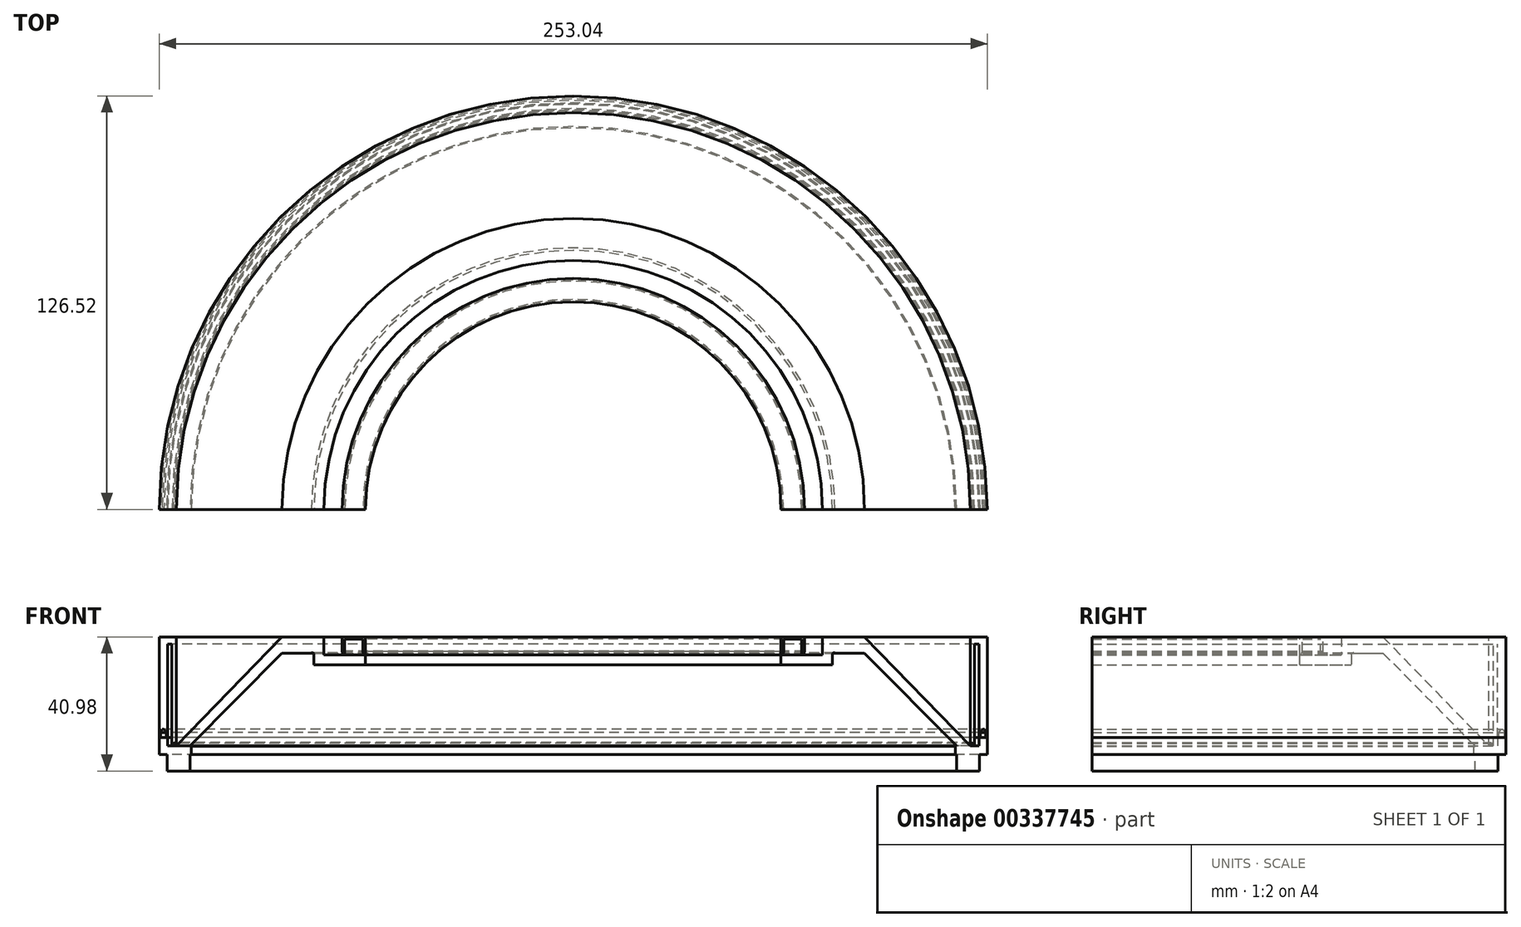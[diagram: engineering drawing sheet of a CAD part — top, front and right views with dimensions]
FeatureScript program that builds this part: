
annotation { "Feature Type Name" : "Feature", "Feature Type Description" : "" }
export const myFeature = defineFeature(function(context is Context, id is Id, definition is map)
    precondition{}
    {
        {
            var Q0;
            Q0=qCreatedBy(makeId("Top.planeOp"),FACE);
            var sketch = newSketch(context, id + "F0", { "sketchPlane" : qUnion([Q0])});
            skCircle(sketch, "E0", {"center": v(0, 0) * mm, "radius": 126.52 * mm});
            skCircle(sketch, "E1", {"center": v(0, 0) * mm, "radius": 124.16 * mm});
            skSolve(sketch);
        }
        {
            var Q0;
            Q0=makeQuery(id+"F0.imprint","IMPRINT",FACE,{"disambiguationData":[TD([[makeQuery(id+"F0.imprint","IMPRINT",EDGE,{"derivedFrom":sQuery(id+"F0.wireOp",EDGE,"E0")}),1.0]])]});
            extrude(context, id + "F1", {"entities" : qUnion([Q0]), "depth" : 2.54 * mm});
        }
        {
            var Q0;
            Q0=makeQuery(id+"F1.opExtrude","CAP_FACE",FACE,{"disambiguationData":[OSD([sQuery(id+"F0.wireOp",EDGE,"E0"),sQuery(id+"F0.wireOp",EDGE,"E1")])],"isStart":true});
            var sketch = newSketch(context, id + "F2", { "sketchPlane" : qUnion([Q0])});
            skCircle(sketch, "E2", {"center": v(0, 0) * mm, "radius": 117.14 * mm});
            skSolve(sketch);
        }
        {
            var Q0;
            Q0=makeQuery(id+"F2.imprint","IMPRINT",FACE,{"disambiguationData":[TD([[makeQuery(id+"F2.imprint","IMPRINT",EDGE,{"derivedFrom":sQuery(id+"F2.wireOp",EDGE,"E2")}),-1.0]])]});
            extrude(context, id + "F3", {"entities" : qUnion([Q0]), "depth" : 5.08 * mm});
        }
        {
            var Q0;
            Q0=makeQuery(id+"F1.opExtrude","CAP_FACE",FACE,{"disambiguationData":[OSD([sQuery(id+"F0.wireOp",EDGE,"E0"),sQuery(id+"F0.wireOp",EDGE,"E1")])],"isStart":false});
            var sketch = newSketch(context, id + "F4", { "sketchPlane" : qUnion([Q0])});
            skCircle(sketch, "E3", {"center": v(0, 0) * mm, "radius": 125.74 * mm});
            skCircle(sketch, "E4", {"center": v(0, 0) * mm, "radius": 116.73 * mm});
            skSolve(sketch);
        }
        {
            var Q0;
            Q0 = qSketchRegion(id + "F4", true);
            extrude(context, id + "F5", {"entities" : qUnion([Q0]), "oppositeDirection" : true, "depth" : 2.54 * mm});
        }
        {
            var Q0;
            Q0=qCreatedBy(makeId("Front.planeOp"),FACE);
            var sketch = newSketch(context, id + "F6", { "sketchPlane" : qUnion([Q0])});
            skLineSegment(sketch, "E5.bottom", {"start": v(-161.42, 99.97) * mm, "end": v(188.15, 99.97) * mm});
            skLineSegment(sketch, "E5.top", {"start": v(-161.42, -119.89) * mm, "end": v(188.15, -119.89) * mm});
            skLineSegment(sketch, "E5.left", {"start": v(-161.42, 99.97) * mm, "end": v(-161.42, -119.89) * mm});
            skLineSegment(sketch, "E5.right", {"start": v(188.15, 99.97) * mm, "end": v(188.15, -119.89) * mm});
            skSolve(sketch);
        }
        {
            var Q0;
            Q0 = qSketchRegion(id + "F6", true);
            extrude(context, id + "F7", {"entities" : qUnion([Q0]), "operationType" : NewBodyOperationType.REMOVE, "depth" : 152.4 * mm});
        }
        {
            var Q0;
            Q0=qCreatedBy(makeId("Front.planeOp"),FACE);
            var sketch = newSketch(context, id + "F8", { "sketchPlane" : qUnion([Q0])});
            skLineSegment(sketch, "E6", {"start": v(0, 0) * mm, "end": v(0, 30.48) * mm});
            skLineSegment(sketch, "E7", {"start": v(63.5, 30.48) * mm, "end": v(76.2, 30.44) * mm});
            skLineSegment(sketch, "E8", {"start": v(76.2, 30.44) * mm, "end": v(76.2, 35.9) * mm});
            skLineSegment(sketch, "E9.1", {"start": v(79.25, 27.38) * mm, "end": v(79.25, 30.55) * mm});
            skLineSegment(sketch, "E9.2", {"start": v(63.5, 27.43) * mm, "end": v(79.25, 27.38) * mm});
            skLineSegment(sketch, "E10", {"start": v(119.67, 0) * mm, "end": v(121.44, 2.5) * mm});
            skLineSegment(sketch, "E11", {"start": v(63.5, 27.43) * mm, "end": v(63.5, 30.48) * mm});
            skLineSegment(sketch, "E12", {"start": v(0, 0) * mm, "end": v(0, -4.78) * mm});
            skPoint(sketch, "E13.visualSharp", {"position": v(79.25, 31.44) * mm});
            skArc(sketch, "E13.filletArc", {"start": v(80.01, 30.99) * mm, "mid": v(79.5, 31) * mm, "end": v(79.25, 30.55) * mm});
            skPoint(sketch, "E14.visualSharp", {"position": v(76.2, 36.79) * mm});
            skLineSegment(sketch, "E15", {"start": v(76.2, 35.9) * mm, "end": v(89.01, 35.9) * mm});
            skLineSegment(sketch, "E16", {"start": v(89.01, 35.9) * mm, "end": v(121.44, 2.5) * mm});
            skLineSegment(sketch, "E17", {"start": v(80.01, 30.99) * mm, "end": v(89.01, 30.96) * mm});
            skLineSegment(sketch, "E18", {"start": v(89.01, 30.96) * mm, "end": v(119.67, 0) * mm});
            skSolve(sketch);
        }
        {
            var Q0;
            Q0 = qSketchRegion(id + "F8", true);
            var Q1;
            Q1=sQuery(id+"F8.wireOp",EDGE,"E6");
            revolve(context, id + "F9", {"operationType" : NewBodyOperationType.ADD, "entities" : qUnion([Q0]), "axis" : qUnion([Q1]), "revolveType" : RevolveType.ONE_DIRECTION, "angle" : 180 * degree});
        }
        {
            var Q0;
            Q0=qCreatedBy(makeId("Front.planeOp"),FACE);
            var sketch = newSketch(context, id + "F10", { "sketchPlane" : qUnion([Q0])});
            skLineSegment(sketch, "E19", {"start": v(123.98, 2.54) * mm, "end": v(126.52, 2.54) * mm});
            skLineSegment(sketch, "E20", {"start": v(126.52, 2.54) * mm, "end": v(126.52, 5.13) * mm});
            skLineSegment(sketch, "E21", {"start": v(123.98, 2.54) * mm, "end": v(123.98, 5.13) * mm});
            skLineSegment(sketch, "E22", {"start": v(126.52, 5.13) * mm, "end": v(123.98, 5.13) * mm});
            skLineSegment(sketch, "E23", {"start": v(0, -2.32) * mm, "end": v(0, -16.42) * mm});
            skSolve(sketch);
        }
        {
            var Q0;
            Q0 = qSketchRegion(id + "F10", true);
            var Q1;
            Q1=sQuery(id+"F10.wireOp",EDGE,"E23");
            revolve(context, id + "F11", {"entities" : qUnion([Q0]), "axis" : qUnion([Q1]), "revolveType" : RevolveType.ONE_DIRECTION, "oppositeDirection" : true, "angle" : 180 * degree});
        }
        {
            var Q0;
            {var subQ0=sQuery(id+"F2.wireOp",EDGE,"E2");var subQ1=sQuery(id+"F0.wireOp",EDGE,"E1");Q0=makeQuery(id+"F7.boolean.opBoolean","COPY",FACE,{"disambiguationData":[TD([makeQuery(id+"F3.opExtrude","SWEPT_FACE",FACE,{"disambiguationData":[OSD([subQ0])]}),makeQuery(id+"F3.opExtrude","CAP_FACE",FACE,{"disambiguationData":[OSD([subQ1,subQ0])],"isStart":true}),makeQuery(id+"F3.opExtrude","CAP_FACE",FACE,{"disambiguationData":[OSD([subQ1,subQ0])],"isStart":false}),makeQuery(id+"F3.opExtrude","SWEPT_FACE",FACE,{"disambiguationData":[OSD([subQ1])]})]),OD(1.0)],"derivedFrom":makeQuery(id+"F7.opExtrude","CAP_FACE",FACE,{"disambiguationData":[OSD([sQuery(id+"F6.wireOp",EDGE,"E5.bottom"),sQuery(id+"F6.wireOp",EDGE,"E5.top"),sQuery(id+"F6.wireOp",EDGE,"E5.left"),sQuery(id+"F6.wireOp",EDGE,"E5.right")])],"isStart":true})});}
            var sketch = newSketch(context, id + "F12", { "sketchPlane" : qUnion([Q0])});
            skLineSegment(sketch, "E24", {"start": v(117.14, 0) * mm, "end": v(117.14, -5.08) * mm});
            skLineSegment(sketch, "E25", {"start": v(117.14, -5.08) * mm, "end": v(124.16, -5.08) * mm});
            skLineSegment(sketch, "E26", {"start": v(124.16, -5.08) * mm, "end": v(124.16, 0) * mm});
            skLineSegment(sketch, "E27", {"start": v(124.16, 0) * mm, "end": v(126.5, 0) * mm});
            skLineSegment(sketch, "E28", {"start": v(126.5, 0) * mm, "end": v(126.5, 5.12) * mm});
            skLineSegment(sketch, "E29", {"start": v(126.5, 5.12) * mm, "end": v(124, 5.12) * mm});
            skLineSegment(sketch, "E30", {"start": v(124, 5.12) * mm, "end": v(124, 2.57) * mm});
            skLineSegment(sketch, "E31", {"start": v(124, 2.57) * mm, "end": v(117.14, 2.57) * mm});
            skLineSegment(sketch, "E32", {"start": v(117.14, 2.57) * mm, "end": v(117.14, 0) * mm});
            skLineSegment(sketch, "E33", {"start": v(0, 0) * mm, "end": v(0, -8.91) * mm});
            skSolve(sketch);
        }
        {
            var Q0;
            Q0 = qSketchRegion(id + "F12", true);
            var Q1;
            Q1=sQuery(id+"F12.wireOp",EDGE,"E33");
            revolve(context, id + "F13", {"operationType" : NewBodyOperationType.ADD, "entities" : qUnion([Q0]), "axis" : qUnion([Q1]), "revolveType" : RevolveType.ONE_DIRECTION, "oppositeDirection" : true, "angle" : 180 * degree});
        }
        {
            var Q0;
            {var subQ0=sQuery(id+"F4.wireOp",EDGE,"E3");var subQ1=sQuery(id+"F4.wireOp",EDGE,"E4");var subQ2=makeQuery(id+"F7.opExtrude","CAP_FACE",FACE,{"disambiguationData":[OSD([sQuery(id+"F6.wireOp",EDGE,"E5.bottom"),sQuery(id+"F6.wireOp",EDGE,"E5.top"),sQuery(id+"F6.wireOp",EDGE,"E5.left"),sQuery(id+"F6.wireOp",EDGE,"E5.right")])],"isStart":true});var subQ3=sQuery(id+"F2.wireOp",EDGE,"E2");var subQ4=sQuery(id+"F0.wireOp",EDGE,"E1");var subQ5=sQuery(id+"F0.wireOp",EDGE,"E0");Q0=makeQuery(id+"F13.boolean.opBoolean","MERGE",FACE,{"derivedFrom":[makeQuery(id+"F7.boolean.opBoolean","COPY",FACE,{"disambiguationData":[TD([makeQuery(id+"F1.opExtrude","SWEPT_FACE",FACE,{"disambiguationData":[OSD([subQ5])]}),makeQuery(id+"F1.opExtrude","CAP_FACE",FACE,{"disambiguationData":[OSD([subQ5,subQ4])],"isStart":true}),makeQuery(id+"F1.opExtrude","CAP_FACE",FACE,{"disambiguationData":[OSD([subQ5,subQ4])],"isStart":false}),makeQuery(id+"F1.opExtrude","SWEPT_FACE",FACE,{"disambiguationData":[OSD([subQ4])]})]),OD(0.0)],"derivedFrom":subQ2}),makeQuery(id+"F7.boolean.opBoolean","COPY",FACE,{"disambiguationData":[TD([makeQuery(id+"F3.opExtrude","SWEPT_FACE",FACE,{"disambiguationData":[OSD([subQ3])]}),makeQuery(id+"F3.opExtrude","CAP_FACE",FACE,{"disambiguationData":[OSD([subQ4,subQ3])],"isStart":true}),makeQuery(id+"F3.opExtrude","CAP_FACE",FACE,{"disambiguationData":[OSD([subQ4,subQ3])],"isStart":false}),makeQuery(id+"F3.opExtrude","SWEPT_FACE",FACE,{"disambiguationData":[OSD([subQ4])]})]),OD(0.0)],"derivedFrom":subQ2}),makeQuery(id+"F9.boolean.opBoolean","MERGE",FACE,{"derivedFrom":[makeQuery(id+"F7.boolean.opBoolean","COPY",FACE,{"disambiguationData":[TD([makeQuery(id+"F5.opExtrude","SWEPT_FACE",FACE,{"disambiguationData":[OSD([subQ0])]}),makeQuery(id+"F5.opExtrude","CAP_FACE",FACE,{"disambiguationData":[OSD([subQ0,subQ1])],"isStart":true}),makeQuery(id+"F5.opExtrude","CAP_FACE",FACE,{"disambiguationData":[OSD([subQ0,subQ1])],"isStart":false}),makeQuery(id+"F5.opExtrude","SWEPT_FACE",FACE,{"disambiguationData":[OSD([subQ1])]})]),OD(0.0)],"derivedFrom":subQ2}),makeQuery(id+"F9.opRevolve","CAP_FACE",FACE,{"disambiguationData":[OSD([sQuery(id+"F8.wireOp",EDGE,"E7"),sQuery(id+"F8.wireOp",EDGE,"E8"),sQuery(id+"F8.wireOp",EDGE,"E9.1"),sQuery(id+"F8.wireOp",EDGE,"E9.2"),sQuery(id+"F8.wireOp",EDGE,"E10"),sQuery(id+"F8.wireOp",EDGE,"E11"),sQuery(id+"F8.wireOp",EDGE,"E13.filletArc"),sQuery(id+"F8.wireOp",EDGE,"E15"),sQuery(id+"F8.wireOp",EDGE,"E16"),sQuery(id+"F8.wireOp",EDGE,"E17"),sQuery(id+"F8.wireOp",EDGE,"E18")])],"isStart":false})]}),makeQuery(id+"F11.opRevolve","CAP_FACE",FACE,{"disambiguationData":[OSD([sQuery(id+"F10.wireOp",EDGE,"E19"),sQuery(id+"F10.wireOp",EDGE,"E20"),sQuery(id+"F10.wireOp",EDGE,"E21"),sQuery(id+"F10.wireOp",EDGE,"E22")])],"isStart":false}),makeQuery(id+"F13.opRevolve","CAP_FACE",FACE,{"disambiguationData":[OSD([sQuery(id+"F12.wireOp",EDGE,"E24"),sQuery(id+"F12.wireOp",EDGE,"E25"),sQuery(id+"F12.wireOp",EDGE,"E26"),sQuery(id+"F12.wireOp",EDGE,"E27"),sQuery(id+"F12.wireOp",EDGE,"E28"),sQuery(id+"F12.wireOp",EDGE,"E29"),sQuery(id+"F12.wireOp",EDGE,"E30"),sQuery(id+"F12.wireOp",EDGE,"E31"),sQuery(id+"F12.wireOp",EDGE,"E32")])],"isStart":false})]});}
            var sketch = newSketch(context, id + "F14", { "sketchPlane" : qUnion([Q0])});
            skLineSegment(sketch, "E34", {"start": v(0, 0) * mm, "end": v(0, 35.9) * mm});
            skLineSegment(sketch, "E35", {"start": v(-63.5, 35.9) * mm, "end": v(-70.65, 35.9) * mm});
            skLineSegment(sketch, "E36.bottom", {"start": v(-63.5, 30.48) * mm, "end": v(-63.9, 30.48) * mm});
            skLineSegment(sketch, "E36.top", {"start": v(-63.5, 35.9) * mm, "end": v(-64.3, 35.9) * mm});
            skLineSegment(sketch, "E36.left", {"start": v(-63.5, 30.48) * mm, "end": v(-63.5, 35.9) * mm});
            skLineSegment(sketch, "E36.right", {"start": v(-64.3, 31.38) * mm, "end": v(-64.3, 35.25) * mm});
            skLineSegment(sketch, "E37.bottom", {"start": v(-69.85, 30.46) * mm, "end": v(-70.25, 30.46) * mm});
            skLineSegment(sketch, "E37.top", {"start": v(-69.85, 35.9) * mm, "end": v(-70.65, 35.9) * mm});
            skLineSegment(sketch, "E37.left", {"start": v(-69.85, 30.46) * mm, "end": v(-69.85, 35.25) * mm});
            skLineSegment(sketch, "E37.right", {"start": v(-70.65, 31.52) * mm, "end": v(-70.65, 35.9) * mm});
            skLineSegment(sketch, "E38", {"start": v(-70.65, 31.52) * mm, "end": v(-70.25, 30.46) * mm});
            skLineSegment(sketch, "E39", {"start": v(-64.3, 31.38) * mm, "end": v(-63.9, 30.48) * mm});
            skLineSegment(sketch, "E40.bottom", {"start": v(-69.85, 35.9) * mm, "end": v(-64.3, 35.9) * mm});
            skLineSegment(sketch, "E40.top", {"start": v(-69.85, 35.25) * mm, "end": v(-64.3, 35.25) * mm});
            skPoint(sketch, "E41.orphan", {"position": v(-70.65, 30.46) * mm});
            skPoint(sketch, "E42.orphan", {"position": v(-64.3, 30.48) * mm});
            skLineSegment(sketch, "E43.bottom", {"start": v(-126.52, 5.13) * mm, "end": v(-126.12, 5.13) * mm});
            skLineSegment(sketch, "E43.top", {"start": v(-126.52, 35.9) * mm, "end": v(-123.98, 35.9) * mm});
            skLineSegment(sketch, "E43.left", {"start": v(-126.52, 5.13) * mm, "end": v(-126.52, 35.9) * mm});
            skLineSegment(sketch, "E43.right", {"start": v(-123.98, 5.13) * mm, "end": v(-123.98, 33.69) * mm});
            skLineSegment(sketch, "E44.top", {"start": v(-121.36, 2.57) * mm, "end": v(-121.76, 2.57) * mm});
            skLineSegment(sketch, "E44.left", {"start": v(-121.36, 2.57) * mm, "end": v(-121.36, 2.57) * mm});
            skLineSegment(sketch, "E44.right", {"start": v(-122.67, 2.57) * mm, "end": v(-122.67, 2.57) * mm});
            skLineSegment(sketch, "E45.bottom", {"start": v(-122.67, 2.57) * mm, "end": v(-122.27, 2.57) * mm});
            skLineSegment(sketch, "E45.top", {"start": v(-122.67, 35.9) * mm, "end": v(-121.36, 35.9) * mm});
            skLineSegment(sketch, "E45.left", {"start": v(-122.67, 2.57) * mm, "end": v(-122.67, 33.69) * mm});
            skLineSegment(sketch, "E45.right", {"start": v(-121.36, 2.57) * mm, "end": v(-121.36, 35.9) * mm});
            skLineSegment(sketch, "E46", {"start": v(-126.12, 5.13) * mm, "end": v(-126.12, 6.62) * mm});
            skLineSegment(sketch, "E47", {"start": v(-126.12, 6.62) * mm, "end": v(-125.65, 7.66) * mm});
            skLineSegment(sketch, "E48", {"start": v(-125.65, 7.66) * mm, "end": v(-125.14, 7.66) * mm});
            skLineSegment(sketch, "E49", {"start": v(-125.14, 7.66) * mm, "end": v(-124.38, 6.62) * mm});
            skLineSegment(sketch, "E50", {"start": v(-124.38, 6.62) * mm, "end": v(-124.38, 5.13) * mm});
            skLineSegment(sketch, "E51.trimOffspring", {"start": v(-124.38, 5.13) * mm, "end": v(-123.98, 5.13) * mm});
            skLineSegment(sketch, "E52", {"start": v(-122.27, 2.57) * mm, "end": v(-122.27, 3.31) * mm});
            skLineSegment(sketch, "E53", {"start": v(-122.27, 3.31) * mm, "end": v(-122.04, 3.6) * mm});
            skLineSegment(sketch, "E54", {"start": v(-122.04, 3.6) * mm, "end": v(-121.76, 3.36) * mm});
            skLineSegment(sketch, "E55", {"start": v(-121.76, 3.36) * mm, "end": v(-121.76, 2.57) * mm});
            skLineSegment(sketch, "E56.bottom", {"start": v(-126.52, 35.9) * mm, "end": v(-121.36, 35.9) * mm});
            skLineSegment(sketch, "E56.top", {"start": v(-123.98, 33.69) * mm, "end": v(-122.67, 33.69) * mm});
            skLineSegment(sketch, "E56.left", {"start": v(-126.52, 35.9) * mm, "end": v(-126.52, 33.69) * mm});
            skLineSegment(sketch, "E56.right", {"start": v(-121.36, 35.9) * mm, "end": v(-121.36, 33.69) * mm});
            skPoint(sketch, "E57.orphan", {"position": v(-130.3, 35.9) * mm});
            skLineSegment(sketch, "E58.trimOffspring", {"start": v(-121.36, 35.9) * mm, "end": v(-126.52, 35.9) * mm});
            skLineSegment(sketch, "E59.trimOffspring", {"start": v(-121.76, 2.57) * mm, "end": v(-121.36, 2.57) * mm});
            skLineSegment(sketch, "E60.trimOffspring", {"start": v(-122.27, 2.57) * mm, "end": v(-122.67, 2.57) * mm});
            skSolve(sketch);
        }
        {
            var Q0;
            Q0 = qSketchRegion(id + "F14", true);
            var Q1;
            Q1=sQuery(id+"F14.wireOp",EDGE,"E34");
            revolve(context, id + "F15", {"entities" : qUnion([Q0]), "axis" : qUnion([Q1]), "revolveType" : RevolveType.ONE_DIRECTION, "oppositeDirection" : true, "angle" : 180 * degree});
        }
    });
